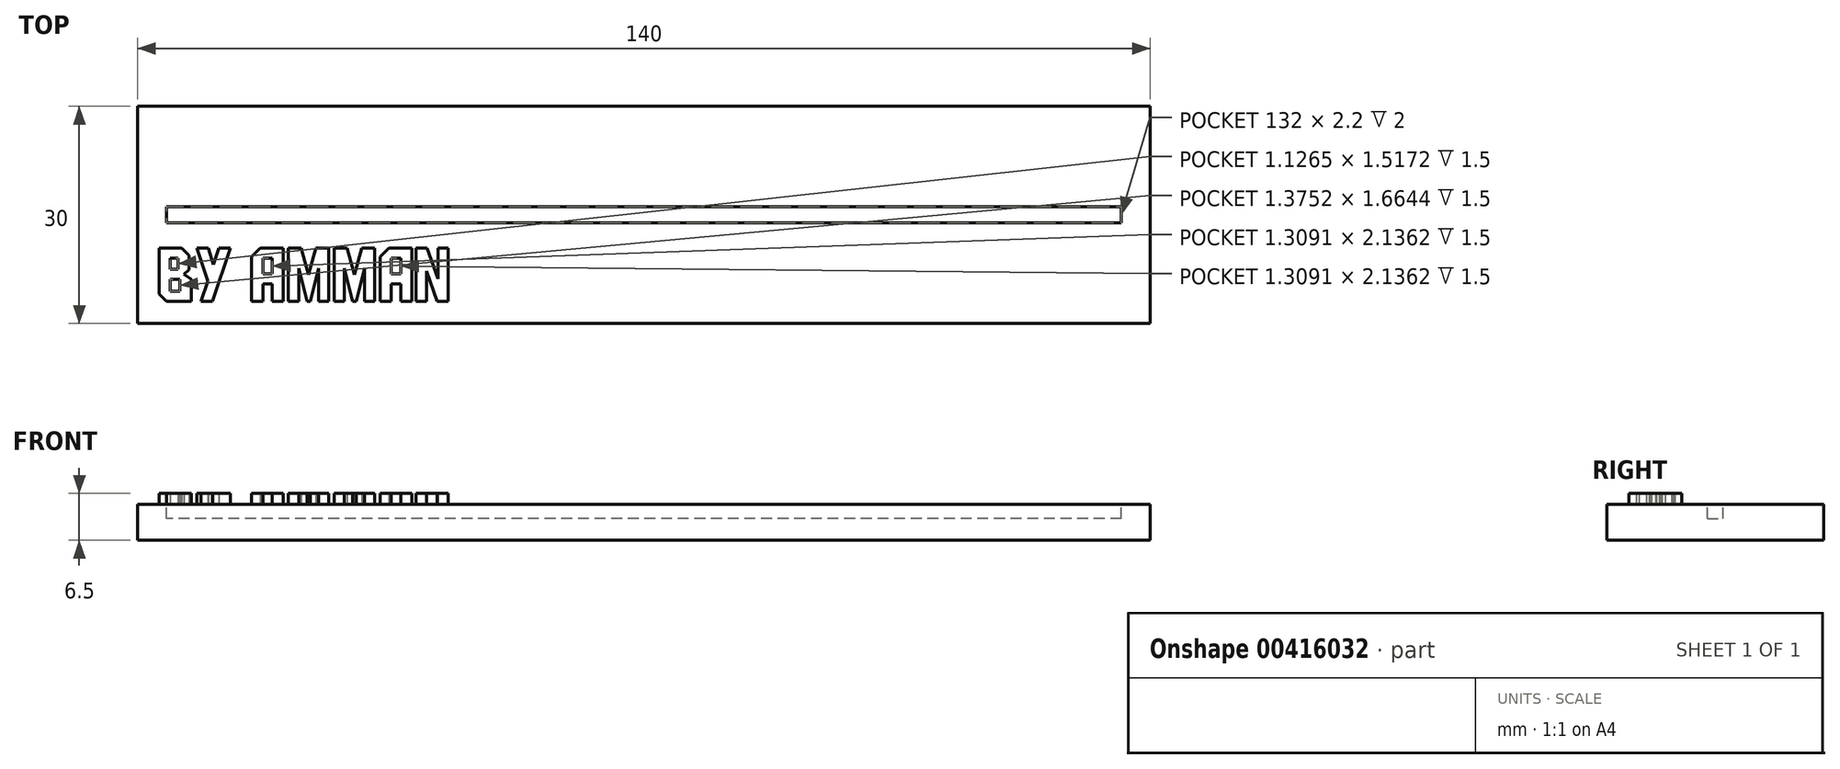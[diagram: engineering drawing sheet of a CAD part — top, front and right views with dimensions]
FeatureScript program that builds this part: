
annotation { "Feature Type Name" : "Feature", "Feature Type Description" : "" }
export const myFeature = defineFeature(function(context is Context, id is Id, definition is map)
    precondition{}
    {
        {
            var Q0;
            Q0=qCreatedBy(makeId("Top.planeOp"),FACE);
            var sketch = newSketch(context, id + "F0", { "sketchPlane" : qUnion([Q0])});
            skLineSegment(sketch, "E0.bottom", {"start": v(70, -15) * mm, "end": v(-70, -15) * mm});
            skLineSegment(sketch, "E0.top", {"start": v(70, 15) * mm, "end": v(-70, 15) * mm});
            skLineSegment(sketch, "E0.left", {"start": v(70, -15) * mm, "end": v(70, 15) * mm});
            skLineSegment(sketch, "E0.right", {"start": v(-70, -15) * mm, "end": v(-70, 15) * mm});
            skPoint(sketch, "E0.middle", {"position": v(0, 0) * mm});
            skSolve(sketch);
        }
        {
            var Q0;
            Q0 = qSketchRegion(id + "F0", true);
            extrude(context, id + "F1", {"entities" : qUnion([Q0]), "depth" : 5 * mm});
        }
        {
            var Q0;
            Q0=makeQuery(id+"F1.opExtrude","CAP_FACE",FACE,{"disambiguationData":[OSD([sQuery(id+"F0.wireOp",EDGE,"E0.bottom"),sQuery(id+"F0.wireOp",EDGE,"E0.top"),sQuery(id+"F0.wireOp",EDGE,"E0.left"),sQuery(id+"F0.wireOp",EDGE,"E0.right")])],"isStart":false});
            var sketch = newSketch(context, id + "F2", { "sketchPlane" : qUnion([Q0])});
            skLineSegment(sketch, "E1.bottom", {"start": v(66, -1.1) * mm, "end": v(-66, -1.1) * mm});
            skLineSegment(sketch, "E1.top", {"start": v(66, 1.1) * mm, "end": v(-66, 1.1) * mm});
            skLineSegment(sketch, "E1.left", {"start": v(66, -1.1) * mm, "end": v(66, 1.1) * mm});
            skLineSegment(sketch, "E1.right", {"start": v(-66, -1.1) * mm, "end": v(-66, 1.1) * mm});
            skPoint(sketch, "E1.middle", {"position": v(0, 0) * mm});
            skSolve(sketch);
        }
        {
            var Q0;
            Q0 = qSketchRegion(id + "F2", true);
            extrude(context, id + "F3", {"entities" : qUnion([Q0]), "operationType" : NewBodyOperationType.REMOVE, "oppositeDirection" : true, "depth" : 2 * mm});
        }
        {
            var Q0;
            Q0=makeQuery(id+"F1.opExtrude","CAP_FACE",FACE,{"disambiguationData":[OSD([sQuery(id+"F0.wireOp",EDGE,"E0.bottom"),sQuery(id+"F0.wireOp",EDGE,"E0.top"),sQuery(id+"F0.wireOp",EDGE,"E0.left"),sQuery(id+"F0.wireOp",EDGE,"E0.right")])],"isStart":false});
            var sketch = newSketch(context, id + "F4", { "sketchPlane" : qUnion([Q0])});
            skLineSegment(sketch, "E2", {"start": v(-62.56, -8.9) * mm, "end": v(-62.56, -11.95) * mm});
            skLineSegment(sketch, "E3", {"start": v(-66, -11.95) * mm, "end": v(-67.01, -10.94) * mm});
            skLineSegment(sketch, "E4", {"start": v(-67.01, -10.94) * mm, "end": v(-67.01, -4.61) * mm});
            skLineSegment(sketch, "E5", {"start": v(-67.01, -4.61) * mm, "end": v(-63.87, -4.61) * mm});
            skLineSegment(sketch, "E6", {"start": v(-63.87, -4.61) * mm, "end": v(-62.83, -5.58) * mm});
            skLineSegment(sketch, "E7", {"start": v(-62.83, -5.58) * mm, "end": v(-62.83, -7.6) * mm});
            skLineSegment(sketch, "E8", {"start": v(-62.83, -7.6) * mm, "end": v(-63.55, -8.18) * mm});
            skLineSegment(sketch, "E9", {"start": v(-63.55, -8.18) * mm, "end": v(-62.56, -8.9) * mm});
            skLineSegment(sketch, "E10", {"start": v(-64.1, -10.56) * mm, "end": v(-64.1, -8.9) * mm});
            skLineSegment(sketch, "E11", {"start": v(-64.1, -8.9) * mm, "end": v(-65.48, -8.9) * mm});
            skLineSegment(sketch, "E12", {"start": v(-65.48, -8.9) * mm, "end": v(-65.48, -10.56) * mm});
            skLineSegment(sketch, "E13", {"start": v(-65.48, -10.56) * mm, "end": v(-64.1, -10.56) * mm});
            skLineSegment(sketch, "E14", {"start": v(-64.35, -7.53) * mm, "end": v(-64.35, -6.01) * mm});
            skLineSegment(sketch, "E15", {"start": v(-64.35, -6.01) * mm, "end": v(-65.48, -6.01) * mm});
            skLineSegment(sketch, "E16", {"start": v(-65.48, -6.01) * mm, "end": v(-65.48, -7.53) * mm});
            skLineSegment(sketch, "E17", {"start": v(-65.48, -7.53) * mm, "end": v(-64.35, -7.53) * mm});
            skLineSegment(sketch, "E18", {"start": v(-58.74, -4.61) * mm, "end": v(-57.14, -4.61) * mm});
            skLineSegment(sketch, "E19", {"start": v(-57.14, -4.61) * mm, "end": v(-59.62, -11.95) * mm});
            skLineSegment(sketch, "E20", {"start": v(-59.62, -11.95) * mm, "end": v(-61.22, -11.95) * mm});
            skLineSegment(sketch, "E21", {"start": v(-61.22, -11.95) * mm, "end": v(-60.27, -9.15) * mm});
            skLineSegment(sketch, "E22", {"start": v(-60.27, -9.15) * mm, "end": v(-61.8, -4.61) * mm});
            skLineSegment(sketch, "E23", {"start": v(-61.8, -4.61) * mm, "end": v(-60.22, -4.61) * mm});
            skLineSegment(sketch, "E24", {"start": v(-60.22, -4.61) * mm, "end": v(-59.51, -6.89) * mm});
            skLineSegment(sketch, "E25", {"start": v(-59.51, -6.89) * mm, "end": v(-58.74, -4.61) * mm});
            skLineSegment(sketch, "E26", {"start": v(-52.65, -11.95) * mm, "end": v(-54.2, -11.95) * mm});
            skLineSegment(sketch, "E27", {"start": v(-54.2, -11.95) * mm, "end": v(-54.2, -5.78) * mm});
            skLineSegment(sketch, "E28", {"start": v(-54.2, -5.78) * mm, "end": v(-53.02, -4.61) * mm});
            skLineSegment(sketch, "E29", {"start": v(-53.02, -4.61) * mm, "end": v(-49.8, -4.61) * mm});
            skLineSegment(sketch, "E30", {"start": v(-49.8, -4.61) * mm, "end": v(-49.8, -11.95) * mm});
            skLineSegment(sketch, "E31", {"start": v(-49.8, -11.95) * mm, "end": v(-51.35, -11.95) * mm});
            skLineSegment(sketch, "E32", {"start": v(-51.35, -11.95) * mm, "end": v(-51.35, -9.54) * mm});
            skLineSegment(sketch, "E33", {"start": v(-51.35, -9.54) * mm, "end": v(-52.65, -9.54) * mm});
            skLineSegment(sketch, "E34", {"start": v(-52.65, -9.54) * mm, "end": v(-52.65, -11.95) * mm});
            skLineSegment(sketch, "E35", {"start": v(-51.35, -8.15) * mm, "end": v(-51.35, -6.01) * mm});
            skLineSegment(sketch, "E36", {"start": v(-51.35, -6.01) * mm, "end": v(-52.65, -6.01) * mm});
            skLineSegment(sketch, "E37", {"start": v(-52.65, -6.01) * mm, "end": v(-52.65, -8.15) * mm});
            skLineSegment(sketch, "E38", {"start": v(-52.65, -8.15) * mm, "end": v(-51.35, -8.15) * mm});
            skLineSegment(sketch, "E39", {"start": v(-45.32, -4.61) * mm, "end": v(-43.54, -4.61) * mm});
            skLineSegment(sketch, "E40", {"start": v(-43.54, -4.61) * mm, "end": v(-43.54, -11.95) * mm});
            skLineSegment(sketch, "E41", {"start": v(-43.54, -11.95) * mm, "end": v(-44.96, -11.95) * mm});
            skLineSegment(sketch, "E42", {"start": v(-44.96, -11.95) * mm, "end": v(-44.96, -7.39) * mm});
            skLineSegment(sketch, "E43", {"start": v(-44.96, -7.39) * mm, "end": v(-46.1, -11.95) * mm});
            skLineSegment(sketch, "E44", {"start": v(-46.1, -11.95) * mm, "end": v(-46.56, -11.95) * mm});
            skLineSegment(sketch, "E45", {"start": v(-46.56, -11.95) * mm, "end": v(-47.7, -7.39) * mm});
            skLineSegment(sketch, "E46", {"start": v(-47.7, -7.39) * mm, "end": v(-47.7, -11.95) * mm});
            skLineSegment(sketch, "E47", {"start": v(-47.7, -11.95) * mm, "end": v(-49.12, -11.95) * mm});
            skLineSegment(sketch, "E48", {"start": v(-49.12, -11.95) * mm, "end": v(-49.12, -4.61) * mm});
            skLineSegment(sketch, "E49", {"start": v(-49.12, -4.61) * mm, "end": v(-47.35, -4.61) * mm});
            skLineSegment(sketch, "E50", {"start": v(-47.35, -4.61) * mm, "end": v(-46.33, -8.27) * mm});
            skLineSegment(sketch, "E51", {"start": v(-46.33, -8.27) * mm, "end": v(-45.32, -4.61) * mm});
            skLineSegment(sketch, "E52", {"start": v(-38.98, -4.61) * mm, "end": v(-37.2, -4.61) * mm});
            skLineSegment(sketch, "E53", {"start": v(-37.2, -4.61) * mm, "end": v(-37.2, -11.95) * mm});
            skLineSegment(sketch, "E54", {"start": v(-37.2, -11.95) * mm, "end": v(-38.62, -11.95) * mm});
            skLineSegment(sketch, "E55", {"start": v(-38.62, -11.95) * mm, "end": v(-38.62, -7.39) * mm});
            skLineSegment(sketch, "E56", {"start": v(-38.62, -7.39) * mm, "end": v(-39.77, -11.95) * mm});
            skLineSegment(sketch, "E57", {"start": v(-39.77, -11.95) * mm, "end": v(-40.22, -11.95) * mm});
            skLineSegment(sketch, "E58", {"start": v(-40.22, -11.95) * mm, "end": v(-41.36, -7.39) * mm});
            skLineSegment(sketch, "E59", {"start": v(-41.36, -7.39) * mm, "end": v(-41.36, -11.95) * mm});
            skLineSegment(sketch, "E60", {"start": v(-41.36, -11.95) * mm, "end": v(-42.79, -11.95) * mm});
            skLineSegment(sketch, "E61", {"start": v(-42.79, -11.95) * mm, "end": v(-42.79, -4.61) * mm});
            skLineSegment(sketch, "E62", {"start": v(-42.79, -4.61) * mm, "end": v(-41, -4.61) * mm});
            skLineSegment(sketch, "E63", {"start": v(-41, -4.61) * mm, "end": v(-40, -8.27) * mm});
            skLineSegment(sketch, "E64", {"start": v(-40, -8.27) * mm, "end": v(-38.98, -4.61) * mm});
            skLineSegment(sketch, "E65", {"start": v(-34.9, -11.95) * mm, "end": v(-36.45, -11.95) * mm});
            skLineSegment(sketch, "E66", {"start": v(-36.45, -11.95) * mm, "end": v(-36.45, -5.78) * mm});
            skLineSegment(sketch, "E67", {"start": v(-36.45, -5.78) * mm, "end": v(-35.27, -4.61) * mm});
            skLineSegment(sketch, "E68", {"start": v(-35.27, -4.61) * mm, "end": v(-32.06, -4.61) * mm});
            skLineSegment(sketch, "E69", {"start": v(-32.06, -4.61) * mm, "end": v(-32.06, -11.95) * mm});
            skLineSegment(sketch, "E70", {"start": v(-32.06, -11.95) * mm, "end": v(-33.6, -11.95) * mm});
            skLineSegment(sketch, "E71", {"start": v(-33.6, -11.95) * mm, "end": v(-33.6, -9.54) * mm});
            skLineSegment(sketch, "E72", {"start": v(-33.6, -9.54) * mm, "end": v(-34.9, -9.54) * mm});
            skLineSegment(sketch, "E73", {"start": v(-34.9, -9.54) * mm, "end": v(-34.9, -11.95) * mm});
            skLineSegment(sketch, "E74", {"start": v(-33.6, -8.15) * mm, "end": v(-33.6, -6.01) * mm});
            skLineSegment(sketch, "E75", {"start": v(-33.6, -6.01) * mm, "end": v(-34.9, -6.01) * mm});
            skLineSegment(sketch, "E76", {"start": v(-34.9, -6.01) * mm, "end": v(-34.9, -8.15) * mm});
            skLineSegment(sketch, "E77", {"start": v(-34.9, -8.15) * mm, "end": v(-33.6, -8.15) * mm});
            skLineSegment(sketch, "E78", {"start": v(-28.47, -8.83) * mm, "end": v(-28.47, -4.61) * mm});
            skLineSegment(sketch, "E79", {"start": v(-28.47, -4.61) * mm, "end": v(-27.01, -4.61) * mm});
            skLineSegment(sketch, "E80", {"start": v(-27.01, -4.61) * mm, "end": v(-27.01, -11.95) * mm});
            skLineSegment(sketch, "E81", {"start": v(-27.01, -11.95) * mm, "end": v(-28.54, -11.95) * mm});
            skLineSegment(sketch, "E82", {"start": v(-28.54, -11.95) * mm, "end": v(-30.04, -7.74) * mm});
            skLineSegment(sketch, "E83", {"start": v(-30.04, -7.74) * mm, "end": v(-30.04, -11.95) * mm});
            skLineSegment(sketch, "E84", {"start": v(-30.04, -11.95) * mm, "end": v(-31.48, -11.95) * mm});
            skLineSegment(sketch, "E85", {"start": v(-31.48, -11.95) * mm, "end": v(-31.48, -4.61) * mm});
            skLineSegment(sketch, "E86", {"start": v(-31.48, -4.61) * mm, "end": v(-29.96, -4.61) * mm});
            skLineSegment(sketch, "E87", {"start": v(-29.96, -4.61) * mm, "end": v(-28.47, -8.83) * mm});
            skLineSegment(sketch, "E88", {"start": v(-66, -11.95) * mm, "end": v(-62.56, -11.95) * mm});
            skSolve(sketch);
        }
        {
            var Q0;
            Q0 = qSketchRegion(id + "F4", true);
            extrude(context, id + "F5", {"entities" : qUnion([Q0]), "operationType" : NewBodyOperationType.ADD, "depth" : 1.5 * mm});
        }
    });
